# Revit family: Gymnasium-Eqpt_Divider-Curtain_IPIbybison_WalkDraw
name_source: partatom
category: Specialty Equipment
revit_build: Autodesk Revit 2018 (Build: 20170927_1515(x64)
units: mm (PartAtom-declared; Revit-internal decimal feet)

## family parameters
Always vertical = Yes
Cut with Voids When Loaded = No
OmniClass Number = 23.40.50.34.17
OmniClass Title = Gymnasium Dividers
Part Type = Normal
Room Calculation Point = No
Round Connector Dimension = Use Diameter
Shared = No

## types (1)
- as Specified
    Available Options = as Specified
    Description = IPI by Bison Manual Pull Divider Curtain - IP810 as Specified
    Expected Lifespan (Years) = 0
    Keynote = 11 66 53
    Maintenance Schedule (Months) = 0
    Manufacturer = IPI by Bison
    Manufacturer Fax = 800-638-0698
    Manufacturer Website = https://ipibybison.com
    Maximum Size = Contact Manufacturer for limits
    Model = IP810
    Product Data = http://www.arcat.com
    Revision = R1_2018-06
    Sales Information = https://ipibybison.com
    URL = https://ipibybison.com
    Warranty Duration (Years) = 0

## geometry (parser evidence)
native form markers: Sweep x4
no freeform markers — native parametric forms only
